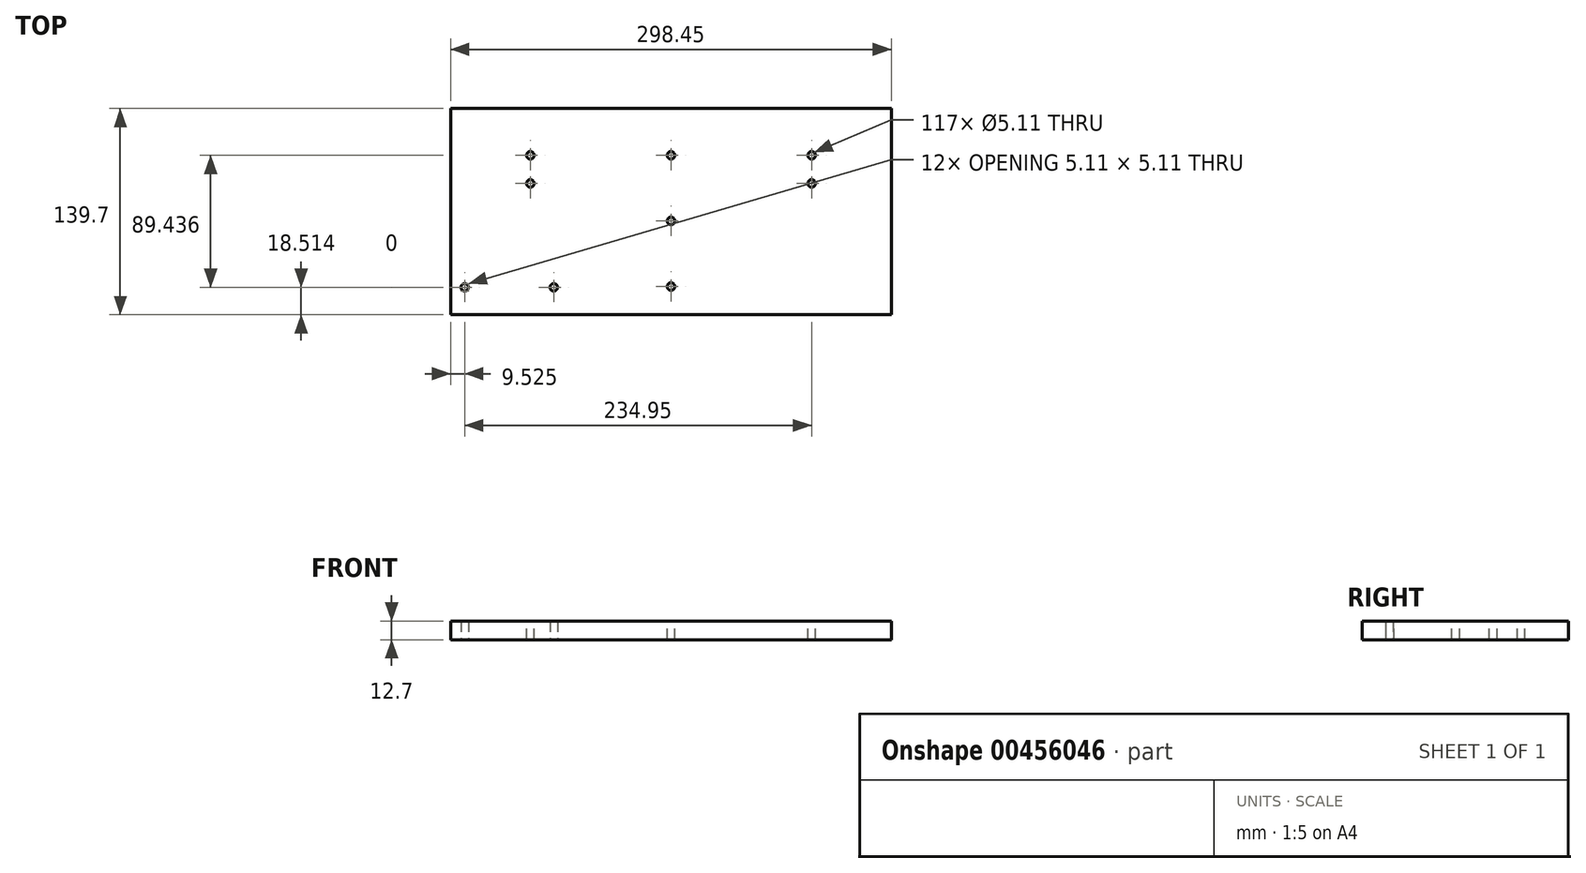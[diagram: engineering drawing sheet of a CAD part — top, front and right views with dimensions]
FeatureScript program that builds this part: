
annotation { "Feature Type Name" : "Feature", "Feature Type Description" : "" }
export const myFeature = defineFeature(function(context is Context, id is Id, definition is map)
    precondition{}
    {
        {
            var Q0;
            Q0=qCreatedBy(makeId("Top.planeOp"),FACE);
            var sketch = newSketch(context, id + "F0", { "sketchPlane" : qUnion([Q0])});
            skLineSegment(sketch, "E0.bottom", {"start": v(0, 0) * mm, "end": v(-298.45, 0) * mm});
            skLineSegment(sketch, "E0.top", {"start": v(0, 127) * mm, "end": v(-298.45, 127) * mm});
            skLineSegment(sketch, "E0.left", {"start": v(0, 0) * mm, "end": v(0, 127) * mm});
            skLineSegment(sketch, "E0.right", {"start": v(-298.45, 0) * mm, "end": v(-298.45, 127) * mm});
            skLineSegment(sketch, "E1", {"start": v(-298.45, 127) * mm, "end": v(-298.45, 139.7) * mm});
            skLineSegment(sketch, "E2", {"start": v(-298.45, 139.7) * mm, "end": v(0, 139.7) * mm});
            skLineSegment(sketch, "E3", {"start": v(0, 139.7) * mm, "end": v(0, 127) * mm});
            skSolve(sketch);
        }
        {
            var Q0;
            Q0=makeQuery(id+"F0.imprint","IMPRINT",FACE,{"disambiguationData":[TD([[makeQuery(id+"F0.imprint","IMPRINT",EDGE,{"derivedFrom":sQuery(id+"F0.wireOp",EDGE,"E0.bottom")}),-1.0]])]});
            var Q1;
            Q1=makeQuery(id+"F0.imprint","IMPRINT",FACE,{"disambiguationData":[TD([[makeQuery(id+"F0.imprint","IMPRINT",EDGE,{"derivedFrom":sQuery(id+"F0.wireOp",EDGE,"E0.top")}),-1.0]])]});
            extrude(context, id + "F1", {"entities" : qUnion([Q0, Q1]), "depth" : 12.7 * mm});
        }
        {
            var Q0;
            Q0=makeQuery(id+"F1.opExtrude","CAP_FACE",FACE,{"disambiguationData":[OSD([sQuery(id+"F0.wireOp",EDGE,"E0.bottom"),sQuery(id+"F0.wireOp",EDGE,"E0.top"),sQuery(id+"F0.wireOp",EDGE,"E0.left"),sQuery(id+"F0.wireOp",EDGE,"E0.right")])],"isStart":false});
            var sketch = newSketch(context, id + "F2", { "sketchPlane" : qUnion([Q0])});
            skLineSegment(sketch, "E4", {"start": v(-149.23, 139.7) * mm, "end": v(-149.22, 0) * mm, "construction": true});
            skPoint(sketch, "E5", {"position": v(-149.22, 107.95) * mm});
            skPoint(sketch, "E6.0.1.0", {"position": v(-149.22, 63.5) * mm});
            skLineSegment(sketch, "E6.direction1", {"start": v(-149.22, 107.95) * mm, "end": v(-123.82, 107.95) * mm, "construction": true});
            skLineSegment(sketch, "E6.direction2", {"start": v(-149.22, 107.95) * mm, "end": v(-149.22, 63.5) * mm, "construction": true});
            skPoint(sketch, "E7.0.0.2", {"position": v(-149.22, 19.05) * mm});
            skSolve(sketch);
        }
        {
            var Q0;
            Q0=sQuery(id+"F2.wireOp",VERTEX,"E5");
            var Q1;
            Q1=sQuery(id+"F2.wireOp",VERTEX,"E6.0.1.0");
            var Q2;
            Q2=sQuery(id+"F2.wireOp",VERTEX,"E7.0.0.2");
            var Q3;
            Q3=makeQuery(id+"F1.opExtrude","SWEPT_BODY",BODY,{"disambiguationData":[OSD([sQuery(id+"F0.wireOp",EDGE,"E0.bottom"),sQuery(id+"F0.wireOp",EDGE,"E0.top"),sQuery(id+"F0.wireOp",EDGE,"E0.left"),sQuery(id+"F0.wireOp",EDGE,"E0.right")])]});
            hole(context, id + "F3", {"style" : HoleStyle.SIMPLE, "endStyle" : HoleEndStyle.THROUGH, "standardTappedOrClearance" : lookupTablePath({ "standard" : "ANSI", "fit" : "Normal (ASME)", "size" : "#10", "type" : "Clearance" }), "standardBlindInLast" : lookupTablePath({ "fit" : "Free", "standard" : "ANSI", "size" : "#10", "type" : "Clearance" }), "holeDiameter" : 5.1 * mm, "isTappedThrough" : true, "tappedDepth" : 8.9 * mm, "tapClearance" : 3, "locations" : qUnion([Q0, Q1, Q2]), "scope" : qUnion([Q3])});
        }
        {
            var Q0;
            Q0=makeQuery(id+"F1.opExtrude","CAP_FACE",FACE,{"disambiguationData":[OSD([sQuery(id+"F0.wireOp",EDGE,"E0.bottom"),sQuery(id+"F0.wireOp",EDGE,"E0.top"),sQuery(id+"F0.wireOp",EDGE,"E0.left"),sQuery(id+"F0.wireOp",EDGE,"E0.right")])],"isStart":false});
            var sketch = newSketch(context, id + "F4", { "sketchPlane" : qUnion([Q0])});
            skPoint(sketch, "E8", {"position": v(-53.98, 107.95) * mm});
            skPoint(sketch, "E9", {"position": v(-53.98, 88.9) * mm});
            skLineSegment(sketch, "E10", {"start": v(-149.23, 139.7) * mm, "end": v(-149.23, 0) * mm, "construction": true});
            skPoint(sketch, "E11.MirrorP", {"position": v(-244.48, 107.95) * mm});
            skPoint(sketch, "E12.MirrorP", {"position": v(-244.48, 88.9) * mm});
            skSolve(sketch);
        }
        {
            var Q0;
            Q0=sQuery(id+"F4.wireOp",VERTEX,"E9");
            var Q1;
            Q1=sQuery(id+"F4.wireOp",VERTEX,"E8");
            var Q2;
            Q2=sQuery(id+"F4.wireOp",VERTEX,"E12.MirrorP");
            var Q3;
            Q3=sQuery(id+"F4.wireOp",VERTEX,"E11.MirrorP");
            var Q4;
            Q4=makeQuery(id+"F1.opExtrude","SWEPT_BODY",BODY,{"disambiguationData":[OSD([sQuery(id+"F0.wireOp",EDGE,"E0.bottom"),sQuery(id+"F0.wireOp",EDGE,"E0.top"),sQuery(id+"F0.wireOp",EDGE,"E0.left"),sQuery(id+"F0.wireOp",EDGE,"E0.right")])]});
            hole(context, id + "F5", {"style" : HoleStyle.SIMPLE, "endStyle" : HoleEndStyle.THROUGH, "standardTappedOrClearance" : lookupTablePath({ "standard" : "ANSI", "fit" : "Normal (ASME)", "size" : "#10", "type" : "Clearance" }), "standardBlindInLast" : lookupTablePath({ "fit" : "Free", "standard" : "ANSI", "size" : "#10", "type" : "Clearance" }), "holeDiameter" : 5.1 * mm, "isTappedThrough" : true, "tappedDepth" : 8.9 * mm, "tapClearance" : 3, "locations" : qUnion([Q0, Q1, Q2, Q3]), "scope" : qUnion([Q4])});
        }
        {
            var Q0;
            Q0=makeQuery(id+"F1.opExtrude","CAP_FACE",FACE,{"disambiguationData":[OSD([sQuery(id+"F0.wireOp",EDGE,"E0.bottom"),sQuery(id+"F0.wireOp",EDGE,"E0.left"),sQuery(id+"F0.wireOp",EDGE,"E0.right"),sQuery(id+"F0.wireOp",EDGE,"E1"),sQuery(id+"F0.wireOp",EDGE,"E2"),sQuery(id+"F0.wireOp",EDGE,"E3")])],"isStart":true});
            var sketch = newSketch(context, id + "F6", { "sketchPlane" : qUnion([Q0])});
            skPoint(sketch, "E13", {"position": v(-288.93, -18.51) * mm});
            skPoint(sketch, "E14", {"position": v(-228.6, -18.51) * mm});
            skSolve(sketch);
        }
        {
            var Q0;
            Q0=sQuery(id+"F6.wireOp",VERTEX,"E13");
            var Q1;
            Q1=sQuery(id+"F6.wireOp",VERTEX,"E14");
            var Q2;
            Q2=makeQuery(id+"F1.opExtrude","SWEPT_BODY",BODY,{"disambiguationData":[OSD([sQuery(id+"F0.wireOp",EDGE,"E0.bottom"),sQuery(id+"F0.wireOp",EDGE,"E0.left"),sQuery(id+"F0.wireOp",EDGE,"E0.right"),sQuery(id+"F0.wireOp",EDGE,"E1"),sQuery(id+"F0.wireOp",EDGE,"E2"),sQuery(id+"F0.wireOp",EDGE,"E3")])]});
            hole(context, id + "F7", {"style" : HoleStyle.SIMPLE, "endStyle" : HoleEndStyle.THROUGH, "standardTappedOrClearance" : lookupTablePath({ "standard" : "ANSI", "fit" : "Normal (ASME)", "size" : "#10", "type" : "Clearance" }), "standardBlindInLast" : lookupTablePath({ "fit" : "Free", "standard" : "ANSI", "size" : "#10", "type" : "Clearance" }), "holeDiameter" : 5.1 * mm, "isTappedThrough" : true, "tappedDepth" : 8.9 * mm, "tapClearance" : 3, "locations" : qUnion([Q0, Q1]), "scope" : qUnion([Q2])});
        }
    });
